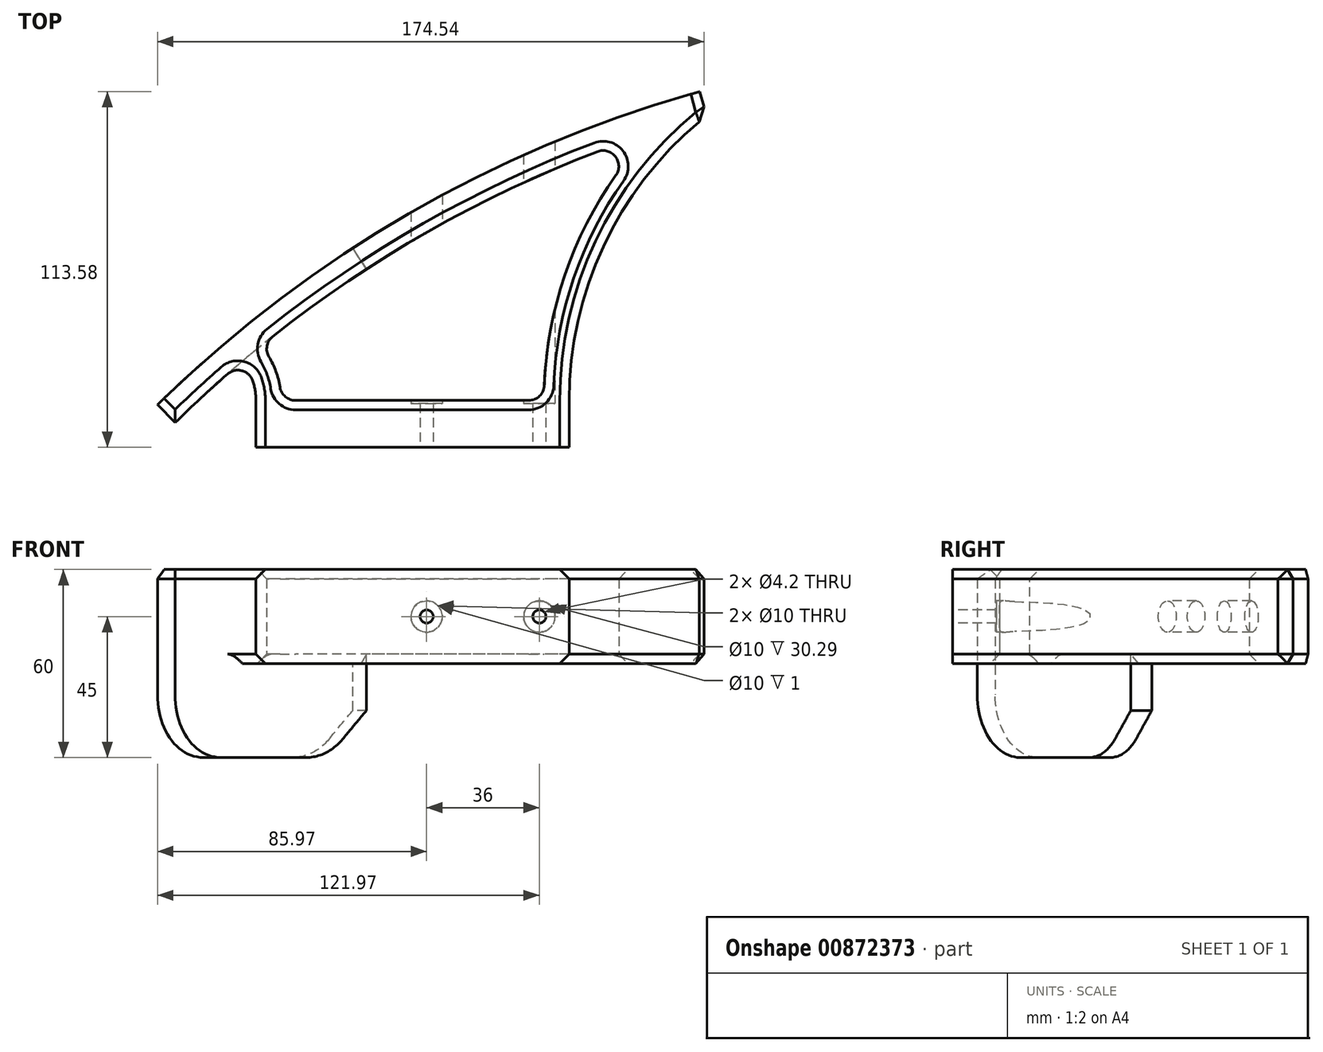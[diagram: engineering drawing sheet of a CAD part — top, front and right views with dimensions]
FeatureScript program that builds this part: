
annotation { "Feature Type Name" : "Feature", "Feature Type Description" : "" }
export const myFeature = defineFeature(function(context is Context, id is Id, definition is map)
    precondition{}
    {
        {
            var Q0;
            Q0=qCreatedBy(makeId("Top.planeOp"),FACE);
            var sketch = newSketch(context, id + "F0", { "sketchPlane" : qUnion([Q0])});
            skLineSegment(sketch, "E0", {"start": v(0, 0) * mm, "end": v(120, 69.28) * mm, "construction": true});
            skLineSegment(sketch, "E1", {"start": v(0, 0) * mm, "end": v(55, 0) * mm, "construction": true});
            skLineSegment(sketch, "E2", {"start": v(55, 0) * mm, "end": v(55, 31.75) * mm, "construction": true});
            skLineSegment(sketch, "E3", {"start": v(98.87, 105.88) * mm, "end": v(120, 69.28) * mm, "construction": true});
            skLineSegment(sketch, "E4", {"start": v(0, 0) * mm, "end": v(55, 0) * mm});
            skLineSegment(sketch, "E5", {"start": v(-76.47, 13.58) * mm, "end": v(96.73, 113.58) * mm, "construction": true});
            skLineSegment(sketch, "E6", {"start": v(0, 0) * mm, "end": v(0, 15) * mm, "construction": true});
            skLineSegment(sketch, "E7", {"start": v(0, 15) * mm, "end": v(55, 15) * mm, "construction": true});
            skArc(sketch, "E8", {"start": v(69.94, 86.87) * mm, "mid": v(53.63, 55) * mm, "end": v(47.1, 19.8) * mm});
            skArc(sketch, "E9.filletArc", {"start": v(42.1, 15) * mm, "mid": v(45.56, 16.4) * mm, "end": v(47.1, 19.8) * mm});
            skLineSegment(sketch, "E10", {"start": v(10.13, 63.58) * mm, "end": v(203.78, -271.83) * mm, "construction": true});
            skArc(sketch, "E11", {"start": v(-76.47, 13.58) * mm, "mid": v(3.78, 74.58) * mm, "end": v(96.73, 113.58) * mm});
            skLineSegment(sketch, "E12", {"start": v(98.87, 105.88) * mm, "end": v(96.73, 113.58) * mm});
            skLineSegment(sketch, "E13", {"start": v(-76.47, 13.58) * mm, "end": v(-70.87, 7.88) * mm});
            skArc(sketch, "E14", {"start": v(98.87, 105.88) * mm, "mid": v(7.78, 67.66) * mm, "end": v(-70.87, 7.88) * mm, "construction": true});
            skArc(sketch, "E15", {"start": v(98.87, 105.88) * mm, "mid": v(66.54, 65.46) * mm, "end": v(55, 15) * mm});
            skLineSegment(sketch, "E16", {"start": v(55, 15) * mm, "end": v(55, 0) * mm});
            skLineSegment(sketch, "E17", {"start": v(-32.4, 15) * mm, "end": v(42.1, 15) * mm});
            skArc(sketch, "E18", {"start": v(69.94, 86.87) * mm, "mid": v(69.82, 92.82) * mm, "end": v(64.08, 94.44) * mm});
            skArc(sketch, "E19", {"start": v(64.08, 94.44) * mm, "mid": v(9.95, 68.9) * mm, "end": v(-39.67, 35.42) * mm});
            skLineSegment(sketch, "E20", {"start": v(0, 0) * mm, "end": v(-45, 0) * mm});
            skLineSegment(sketch, "E21", {"start": v(-45, 0) * mm, "end": v(-45, 15) * mm});
            skLineSegment(sketch, "E22", {"start": v(-45, 15) * mm, "end": v(0, 15) * mm, "construction": true});
            skLineSegment(sketch, "E23", {"start": v(27.5, 0) * mm, "end": v(27.5, 15) * mm, "construction": true});
            skArc(sketch, "E24", {"start": v(-37.33, 19.22) * mm, "mid": v(-35.64, 16.2) * mm, "end": v(-32.4, 15) * mm});
            skArc(sketch, "E25", {"start": v(-37.33, 19.22) * mm, "mid": v(-38.63, 24.24) * mm, "end": v(-40.85, 28.93) * mm});
            skArc(sketch, "E26", {"start": v(-39.67, 35.42) * mm, "mid": v(-41.48, 32.4) * mm, "end": v(-40.85, 28.93) * mm});
            skArc(sketch, "E27", {"start": v(-49.52, 27.34) * mm, "mid": v(-60.37, 17.8) * mm, "end": v(-70.87, 7.88) * mm});
            skArc(sketch, "E28", {"start": v(-45, 15) * mm, "mid": v(-46.17, 21.57) * mm, "end": v(-49.52, 27.34) * mm});
            skLineSegment(sketch, "E29", {"start": v(-49.52, 27.34) * mm, "end": v(203.78, -271.83) * mm, "construction": true});
            skSolve(sketch);
        }
        {
            var Q0;
            Q0=makeQuery(id+"F0.imprint","IMPRINT",FACE,{"disambiguationData":[TD([[makeQuery(id+"F0.imprint","IMPRINT",EDGE,{"derivedFrom":sQuery(id+"F0.wireOp",EDGE,"E4")}),1.0]])]});
            extrude(context, id + "F1", {"entities" : qUnion([Q0]), "depth" : 30 * mm, "offsetDistance" : 25 * mm});
        }
        {
            var Q0;
            Q0=makeQuery(id+"F1.opExtrude","SWEPT_FACE",FACE,{"disambiguationData":[OSD([sQuery(id+"F0.wireOp",EDGE,"E4")])]});
            var sketch = newSketch(context, id + "F2", { "sketchPlane" : qUnion([Q0])});
            skLineSegment(sketch, "E30", {"start": v(55, 15) * mm, "end": v(55, 15) * mm});
            skLineSegment(sketch, "E31", {"start": v(27.5, 30) * mm, "end": v(27.5, 0) * mm, "construction": true});
            skCircle(sketch, "E32", {"center": v(45.5, 15) * mm, "radius": 2.1 * mm});
            skCircle(sketch, "E33", {"center": v(9.5, 15) * mm, "radius": 2.1 * mm});
            skSolve(sketch);
        }
        {
            var Q0;
            Q0=qSketchRegion(id+"F2",true);
            extrude(context, id + "F3", {"entities" : qUnion([Q0]), "operationType" : NewBodyOperationType.REMOVE, "endBound" : BoundingType.THROUGH_ALL, "oppositeDirection" : true, "depth" : 25 * mm, "offsetDistance" : 25 * mm});
        }
        {
            var Q0;
            Q0=makeQuery(id+"F1.opExtrude","SWEPT_FACE",FACE,{"disambiguationData":[OSD([sQuery(id+"F0.wireOp",EDGE,"E17")])]});
            var sketch = newSketch(context, id + "F4", { "sketchPlane" : qUnion([Q0])});
            skCircle(sketch, "E34", {"center": v(-45.5, 15) * mm, "radius": 5 * mm});
            skCircle(sketch, "E35", {"center": v(-9.5, 15) * mm, "radius": 5 * mm});
            skSolve(sketch);
        }
        {
            var Q0;
            Q0=qSketchRegion(id+"F4",true);
            extrude(context, id + "F5", {"entities" : qUnion([Q0]), "operationType" : NewBodyOperationType.REMOVE, "endBound" : BoundingType.THROUGH_ALL, "depth" : 25 * mm, "offsetDistance" : 25 * mm, "hasSecondDirection" : true, "secondDirectionOppositeDirection" : true, "secondDirectionDepth" : 1 * mm});
        }
        {
            var Q0;
            Q0=makeQuery(id+"F0.imprint","IMPRINT",FACE,{"disambiguationData":[TD([[makeQuery(id+"F0.imprint","IMPRINT",EDGE,{"derivedFrom":sQuery(id+"F0.wireOp",EDGE,"E4")}),1.0]])]});
            var sketch = newSketch(context, id + "F6", { "sketchPlane" : qUnion([Q0])});
            skArc(sketch, "E36", {"start": v(-9.72, 56.94) * mm, "mid": v(-41.52, 33.94) * mm, "end": v(-70.87, 7.88) * mm});
            skArc(sketch, "E37", {"start": v(-14.07, 63.64) * mm, "mid": v(-46.53, 40.18) * mm, "end": v(-76.47, 13.58) * mm});
            skLineSegment(sketch, "E38", {"start": v(-70.87, 7.88) * mm, "end": v(-76.47, 13.58) * mm});
            skLineSegment(sketch, "E39", {"start": v(-9.72, 56.94) * mm, "end": v(-14.07, 63.64) * mm});
            skSolve(sketch);
        }
        {
            var Q0;
            Q0 = qSketchRegion(id + "F6", true);
            extrude(context, id + "F7", {"entities" : qUnion([Q0]), "operationType" : NewBodyOperationType.ADD, "oppositeDirection" : true, "depth" : 30 * mm, "offsetDistance" : 25 * mm});
        }
        {
            var Q0;
            Q0=makeQuery(id+"F1.opExtrude","SWEPT_EDGE",EDGE,{"disambiguationData":[OSD([sQuery(id+"F0.wireOp",EDGE,"E27"),sQuery(id+"F0.wireOp",EDGE,"E28")])]});
            fillet(context, id + "F8", {"entities" : qUnion([Q0]), "radius" : 5 * mm, "tangentPropagation" : true, "allowEdgeOverflow" : false});
        }
        {
            var Q0;
            Q0=makeQuery(id+"F7.opExtrude","CAP_EDGE",EDGE,{"disambiguationData":[OSD([sQuery(id+"F6.wireOp",EDGE,"E39")])],"isStart":false});
            var Q1;
            Q1=makeQuery(id+"F7.opExtrude","CAP_EDGE",EDGE,{"disambiguationData":[OSD([sQuery(id+"F6.wireOp",EDGE,"E39")])],"isStart":true});
            chamfer(context, id + "F9", {"entities" : qUnion([Q0, Q1]), "width" : 15 * mm, "tangentPropagation" : true});
        }
        {
            var Q0;
            Q0=makeQuery(id+"F9.opChamfer","BLEND_EDGE",EDGE,{"blendedFrom":[makeQuery(id+"F7.opExtrude","CAP_EDGE",EDGE,{"disambiguationData":[OSD([sQuery(id+"F6.wireOp",EDGE,"E39")])],"isStart":true}),makeQuery(id+"F1.opExtrude","CAP_FACE",FACE,{"disambiguationData":[OSD([sQuery(id+"F0.wireOp",EDGE,"E4"),sQuery(id+"F0.wireOp",EDGE,"E8"),sQuery(id+"F0.wireOp",EDGE,"E9.filletArc"),sQuery(id+"F0.wireOp",EDGE,"E11"),sQuery(id+"F0.wireOp",EDGE,"E12"),sQuery(id+"F0.wireOp",EDGE,"E13"),sQuery(id+"F0.wireOp",EDGE,"E15"),sQuery(id+"F0.wireOp",EDGE,"E16"),sQuery(id+"F0.wireOp",EDGE,"E17"),sQuery(id+"F0.wireOp",EDGE,"E18"),sQuery(id+"F0.wireOp",EDGE,"E19"),sQuery(id+"F0.wireOp",EDGE,"E20"),sQuery(id+"F0.wireOp",EDGE,"E21"),sQuery(id+"F0.wireOp",EDGE,"E24"),sQuery(id+"F0.wireOp",EDGE,"E25"),sQuery(id+"F0.wireOp",EDGE,"E26"),sQuery(id+"F0.wireOp",EDGE,"E27"),sQuery(id+"F0.wireOp",EDGE,"E28")])],"isStart":true})],"blendedInto":[makeQuery(id+"F1.opExtrude","CAP_FACE",FACE,{"disambiguationData":[OSD([sQuery(id+"F0.wireOp",EDGE,"E4"),sQuery(id+"F0.wireOp",EDGE,"E8"),sQuery(id+"F0.wireOp",EDGE,"E9.filletArc"),sQuery(id+"F0.wireOp",EDGE,"E11"),sQuery(id+"F0.wireOp",EDGE,"E12"),sQuery(id+"F0.wireOp",EDGE,"E13"),sQuery(id+"F0.wireOp",EDGE,"E15"),sQuery(id+"F0.wireOp",EDGE,"E16"),sQuery(id+"F0.wireOp",EDGE,"E17"),sQuery(id+"F0.wireOp",EDGE,"E18"),sQuery(id+"F0.wireOp",EDGE,"E19"),sQuery(id+"F0.wireOp",EDGE,"E20"),sQuery(id+"F0.wireOp",EDGE,"E21"),sQuery(id+"F0.wireOp",EDGE,"E24"),sQuery(id+"F0.wireOp",EDGE,"E25"),sQuery(id+"F0.wireOp",EDGE,"E26"),sQuery(id+"F0.wireOp",EDGE,"E27"),sQuery(id+"F0.wireOp",EDGE,"E28")])],"isStart":true})]});
            var Q1;
            {var subQ0=sQuery(id+"F6.wireOp",EDGE,"E39");Q1=makeQuery(id+"F9.opChamfer","BLEND_EDGE",EDGE,{"blendedFrom":[makeQuery(id+"F7.opExtrude","CAP_EDGE",EDGE,{"disambiguationData":[OSD([subQ0])],"isStart":false}),makeQuery(id+"F7.opExtrude","CAP_FACE",FACE,{"disambiguationData":[OSD([sQuery(id+"F6.wireOp",EDGE,"E36"),sQuery(id+"F6.wireOp",EDGE,"E37"),sQuery(id+"F6.wireOp",EDGE,"E38"),subQ0])],"isStart":false})],"blendedInto":[makeQuery(id+"F7.opExtrude","CAP_FACE",FACE,{"disambiguationData":[OSD([sQuery(id+"F6.wireOp",EDGE,"E36"),sQuery(id+"F6.wireOp",EDGE,"E37"),sQuery(id+"F6.wireOp",EDGE,"E38"),subQ0])],"isStart":false})]});}
            var Q2;
            Q2=makeQuery(id+"F7.opExtrude","CAP_EDGE",EDGE,{"disambiguationData":[OSD([sQuery(id+"F6.wireOp",EDGE,"E38")])],"isStart":false});
            fillet(context, id + "F10", {"entities" : qUnion([Q0, Q1, Q2]), "radius" : 20 * mm, "tangentPropagation" : true, "allowEdgeOverflow" : false});
        }
        {
            var Q0;
            Q0=makeQuery(id+"F1.opExtrude","CAP_EDGE",EDGE,{"disambiguationData":[OSD([sQuery(id+"F0.wireOp",EDGE,"E21")])],"isStart":true});
            var Q1;
            Q1=makeQuery(id+"F1.opExtrude","CAP_EDGE",EDGE,{"disambiguationData":[OSD([sQuery(id+"F0.wireOp",EDGE,"E21")])],"isStart":false});
            var Q2;
            Q2=makeQuery(id+"F1.opExtrude","CAP_EDGE",EDGE,{"disambiguationData":[OSD([sQuery(id+"F0.wireOp",EDGE,"E17")])],"isStart":true});
            var Q3;
            Q3=makeQuery(id+"F1.opExtrude","CAP_EDGE",EDGE,{"disambiguationData":[OSD([sQuery(id+"F0.wireOp",EDGE,"E15")])],"isStart":true});
            var Q4;
            Q4=makeQuery(id+"F1.opExtrude","CAP_EDGE",EDGE,{"disambiguationData":[OSD([sQuery(id+"F0.wireOp",EDGE,"E15")])],"isStart":false});
            var Q5;
            Q5=makeQuery(id+"F1.opExtrude","CAP_EDGE",EDGE,{"disambiguationData":[OSD([sQuery(id+"F0.wireOp",EDGE,"E17")])],"isStart":false});
            var Q6;
            Q6=makeQuery(id+"F1.opExtrude","CAP_EDGE",EDGE,{"disambiguationData":[OSD([sQuery(id+"F0.wireOp",EDGE,"E12")])],"isStart":false});
            var Q7;
            Q7=makeQuery(id+"F1.opExtrude","CAP_EDGE",EDGE,{"disambiguationData":[OSD([sQuery(id+"F0.wireOp",EDGE,"E12")])],"isStart":true});
            var Q8;
            Q8=makeQuery(id+"F1.opExtrude","SWEPT_EDGE",EDGE,{"disambiguationData":[OSD([sQuery(id+"F0.wireOp",EDGE,"E12"),sQuery(id+"F0.wireOp",EDGE,"E15")])]});
            var Q9;
            Q9=makeQuery(id+"F1.opExtrude","CAP_EDGE",EDGE,{"disambiguationData":[OSD([sQuery(id+"F0.wireOp",EDGE,"E13")])],"isStart":false});
            var Q10;
            Q10=makeQuery(id+"F1.opExtrude","CAP_EDGE",EDGE,{"disambiguationData":[OSD([sQuery(id+"F0.wireOp",EDGE,"E27")])],"isStart":false});
            chamfer(context, id + "F11", {"entities" : qUnion([Q0, Q1, Q2, Q3, Q4, Q5, Q6, Q7, Q8, Q9, Q10]), "width" : 3 * mm, "tangentPropagation" : true});
        }
    });
